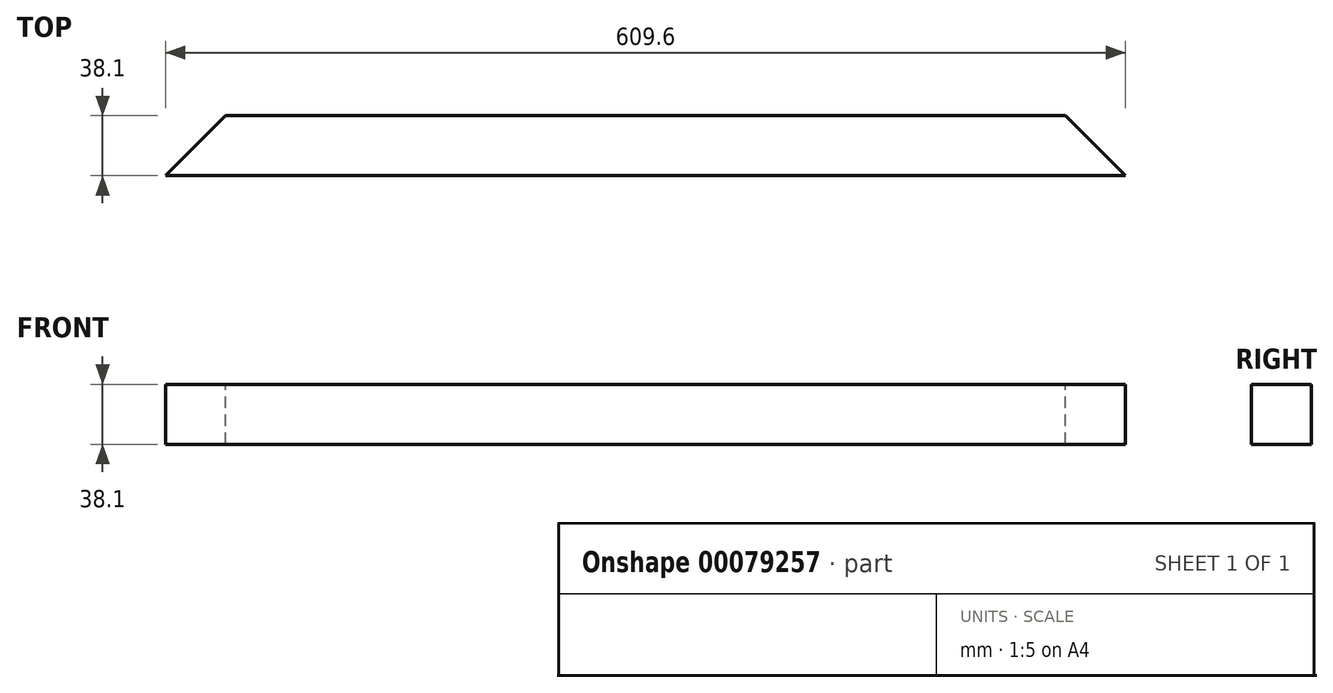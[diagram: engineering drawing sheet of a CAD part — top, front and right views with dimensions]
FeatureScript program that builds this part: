
annotation { "Feature Type Name" : "Feature", "Feature Type Description" : "" }
export const myFeature = defineFeature(function(context is Context, id is Id, definition is map)
    precondition{}
    {
        {
            var Q0;
            Q0=qCreatedBy(makeId("Right.planeOp"),FACE);
            var sketch = newSketch(context, id + "F0", { "sketchPlane" : qUnion([Q0])});
            skLineSegment(sketch, "E0.bottom", {"start": v(0, 0) * mm, "end": v(38.1, 0) * mm});
            skLineSegment(sketch, "E0.top", {"start": v(0, 38.1) * mm, "end": v(38.1, 38.1) * mm});
            skLineSegment(sketch, "E0.left", {"start": v(0, 0) * mm, "end": v(0, 38.1) * mm});
            skLineSegment(sketch, "E0.right", {"start": v(38.1, 0) * mm, "end": v(38.1, 38.1) * mm});
            skSolve(sketch);
        }
        {
            var Q0;
            Q0=makeQuery(id+"F0.imprint","IMPRINT",FACE,{"disambiguationData":[TD([[makeQuery(id+"F0.imprint","IMPRINT",EDGE,{"derivedFrom":sQuery(id+"F0.wireOp",EDGE,"E0.bottom")}),1.0]])]});
            extrude(context, id + "F1", {"entities" : qUnion([Q0]), "depth" : 609.6 * mm});
        }
        {
            var Q0;
            Q0=makeQuery(id+"F1.opExtrude","SWEPT_FACE",FACE,{"disambiguationData":[OSD([sQuery(id+"F0.wireOp",EDGE,"E0.top")])]});
            var sketch = newSketch(context, id + "F2", { "sketchPlane" : qUnion([Q0])});
            skLineSegment(sketch, "E1", {"start": v(0, 0) * mm, "end": v(0, 38.1) * mm});
            skLineSegment(sketch, "E2", {"start": v(0, 38.1) * mm, "end": v(38.1, 38.1) * mm});
            skLineSegment(sketch, "E3", {"start": v(38.1, 38.1) * mm, "end": v(0, 0) * mm});
            skLineSegment(sketch, "E4", {"start": v(609.6, 0) * mm, "end": v(609.6, 38.1) * mm});
            skLineSegment(sketch, "E5", {"start": v(609.6, 38.1) * mm, "end": v(571.5, 38.1) * mm});
            skLineSegment(sketch, "E6", {"start": v(571.5, 38.1) * mm, "end": v(609.6, 0) * mm});
            skSolve(sketch);
        }
        {
            var Q0;
            Q0=makeQuery(id+"F2.imprint","IMPRINT",FACE,{"disambiguationData":[TD([[makeQuery(id+"F2.imprint","IMPRINT",EDGE,{"derivedFrom":sQuery(id+"F2.wireOp",EDGE,"E1")}),-1.0]])]});
            var Q1;
            Q1=makeQuery(id+"F2.imprint","IMPRINT",FACE,{"disambiguationData":[TD([[makeQuery(id+"F2.imprint","IMPRINT",EDGE,{"derivedFrom":sQuery(id+"F2.wireOp",EDGE,"E4")}),1.0]])]});
            extrude(context, id + "F3", {"entities" : qUnion([Q0, Q1]), "operationType" : NewBodyOperationType.REMOVE, "oppositeDirection" : true, "depth" : 38.1 * mm});
        }
    });
